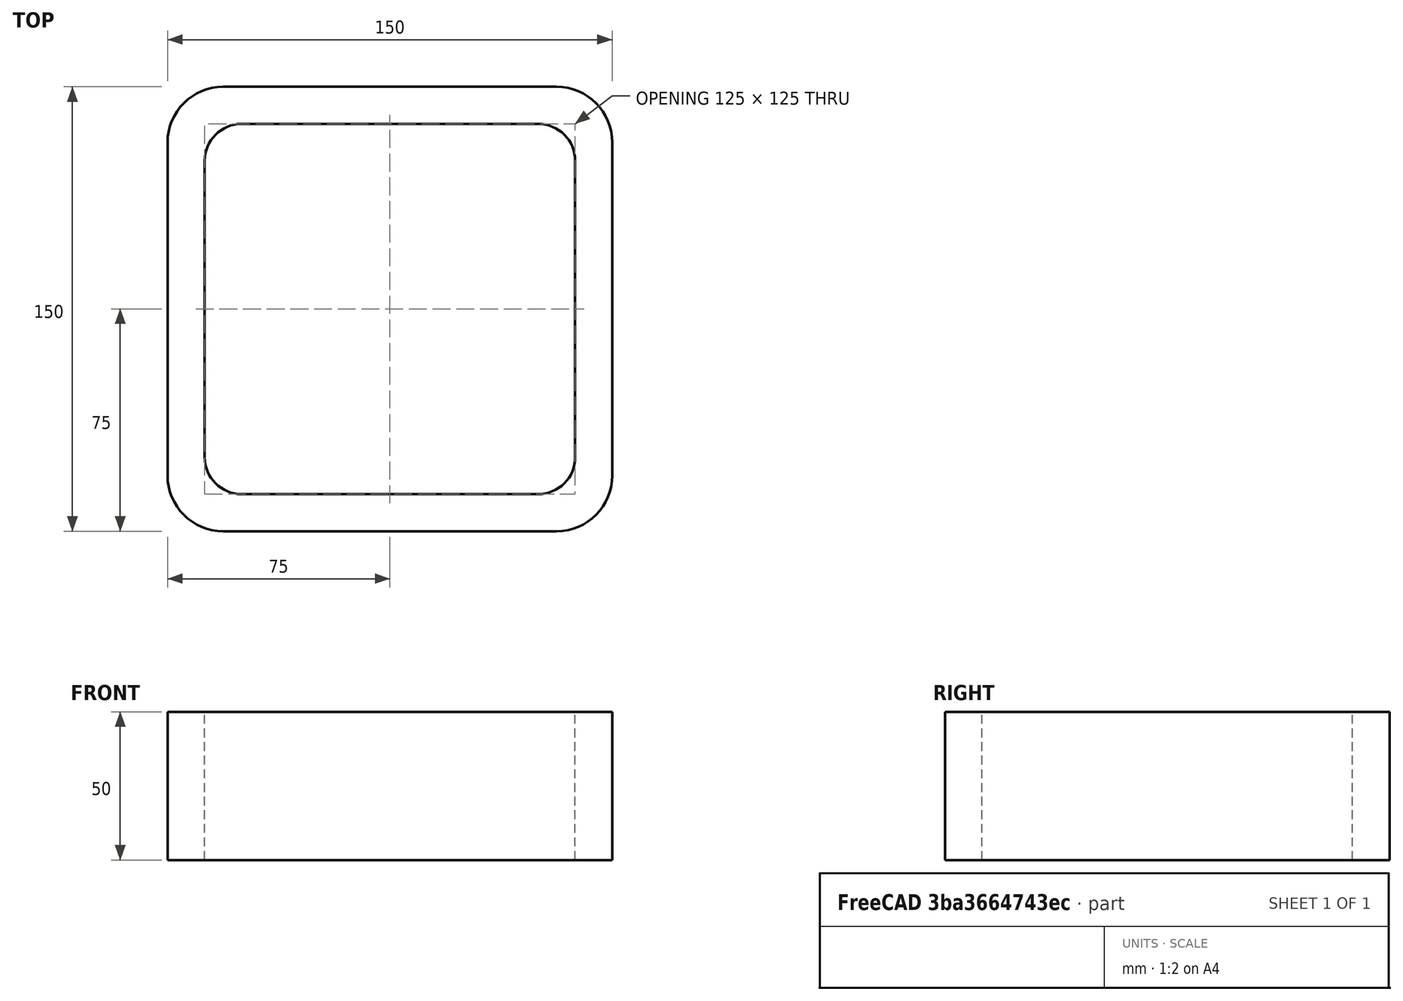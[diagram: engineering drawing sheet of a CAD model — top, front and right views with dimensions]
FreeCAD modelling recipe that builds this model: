
FCSTD DOCUMENT  (FreeCAD 0.15R4671 (Git))
Label: Square hollow section 150x150x12.5 EN10219 S235JRH
License: All rights reserved
LicenseURL: http://en.wikipedia.org/wiki/All_rights_reserved
objects: Sketcher::SketchObject×1, Part::Extrusion×1
note: 2 computed .brp shape members not serialized (recipe doc carries the construction recipe); baked Part::Feature solids carry a one-line shape summary decoded from their .brp

FEATURE [Sketcher::SketchObject] Sketch
  sketch-geometry (16):
    g0: LineSegment StartX=-50 StartY=62.5 StartZ=0 EndX=50 EndY=62.5 EndZ=0
    g1: LineSegment StartX=62.5 StartY=50 StartZ=0 EndX=62.5 EndY=-50 EndZ=0
    g2: LineSegment StartX=50 StartY=-62.5 StartZ=0 EndX=-50 EndY=-62.5 EndZ=0
    g3: LineSegment StartX=-62.5 StartY=-50 StartZ=0 EndX=-62.5 EndY=50 EndZ=0
    g4: LineSegment StartX=-56.25 StartY=75 StartZ=0 EndX=56.25 EndY=75 EndZ=0
    g5: LineSegment StartX=75 StartY=56.25 StartZ=0 EndX=75 EndY=-56.25 EndZ=0
    g6: LineSegment StartX=56.25 StartY=-75 StartZ=0 EndX=-56.25 EndY=-75 EndZ=0
    g7: LineSegment StartX=-75 StartY=-56.25 StartZ=0 EndX=-75 EndY=56.25 EndZ=0
    g8: ArcOfCircle CenterX=-50 CenterY=50 CenterZ=0 NormalX=0 NormalY=0 NormalZ=1 Radius=12.5 StartAngle=1.5708 EndAngle=3.14159
    g9: ArcOfCircle CenterX=50 CenterY=50 CenterZ=0 NormalX=0 NormalY=0 NormalZ=1 Radius=12.5 StartAngle=0 EndAngle=1.5708
    g10: ArcOfCircle CenterX=50 CenterY=-50 CenterZ=0 NormalX=0 NormalY=0 NormalZ=1 Radius=12.5 StartAngle=4.71239 EndAngle=6.28319
    g11: ArcOfCircle CenterX=-50 CenterY=-50 CenterZ=0 NormalX=0 NormalY=0 NormalZ=1 Radius=12.5 StartAngle=3.14159 EndAngle=4.71239
    g12: ArcOfCircle CenterX=56.25 CenterY=56.25 CenterZ=0 NormalX=0 NormalY=0 NormalZ=1 Radius=18.75 StartAngle=0 EndAngle=1.5708
    g13: ArcOfCircle CenterX=56.25 CenterY=-56.25 CenterZ=0 NormalX=0 NormalY=0 NormalZ=1 Radius=18.75 StartAngle=4.71239 EndAngle=6.28319
    g14: ArcOfCircle CenterX=-56.25 CenterY=-56.25 CenterZ=0 NormalX=0 NormalY=0 NormalZ=1 Radius=18.75 StartAngle=3.14159 EndAngle=4.71239
    g15: ArcOfCircle CenterX=-56.25 CenterY=56.25 CenterZ=0 NormalX=0 NormalY=0 NormalZ=1 Radius=18.75 StartAngle=1.5708 EndAngle=3.14159
  constraints (36):
    c: Horizontal(g2)
    c: Vertical(g3)
    c: Horizontal(g6)
    c: Vertical(g7)
    c: Tangent(g3,g8) = 1.5708
    c: Tangent(g0,g8) = 1.5708
    c: Tangent(g0,g9) = 1.5708
    c: Tangent(g1,g9) = 1.5708
    c: Tangent(g1,g10) = 1.5708
    c: Tangent(g2,g10) = 1.5708
    c: Tangent(g2,g11) = 1.5708
    c: Tangent(g3,g11) = 1.5708
    c: Tangent(g4,g12) = 1.5708
    c: Tangent(g5,g12) = 1.5708
    c: Tangent(g5,g13) = 1.5708
    c: Tangent(g6,g13) = 1.5708
    c: Tangent(g6,g14) = 1.5708
    c: Tangent(g7,g14) = 1.5708
    c: Tangent(g7,g15) = 1.5708
    c: Tangent(g4,g15) = 1.5708
    c: Equal(g9,g8)
    c: Equal(g9,g11)
    c: Equal(g9,g10)
    c: Equal(g12,g15)
    c: Equal(g12,g14)
    c: Equal(g12,g13)
    c: Symmetric(g4,g6,g-1)
    c: Symmetric(g7,g5,g-2)
    c: DistanceY(g4,g6) = -150
    c: DistanceX(g7,g5) = 150
    c: Symmetric(g3,g1,g-2)
    c: Symmetric(g0,g2,g-1)
    c: DistanceY(g0,g4) = 12.5
    c: DistanceX(g5,g1) = -12.5
    c: Radius(g9) = 12.5
    c: Radius(g12) = 18.75
FEATURE [Part::Extrusion] Extrude  label="Square hollow section 150x150x12.5 EN10219 S235JRH"
  Base = -> Sketch
  Dir = (0,0,50)
  Solid = true
